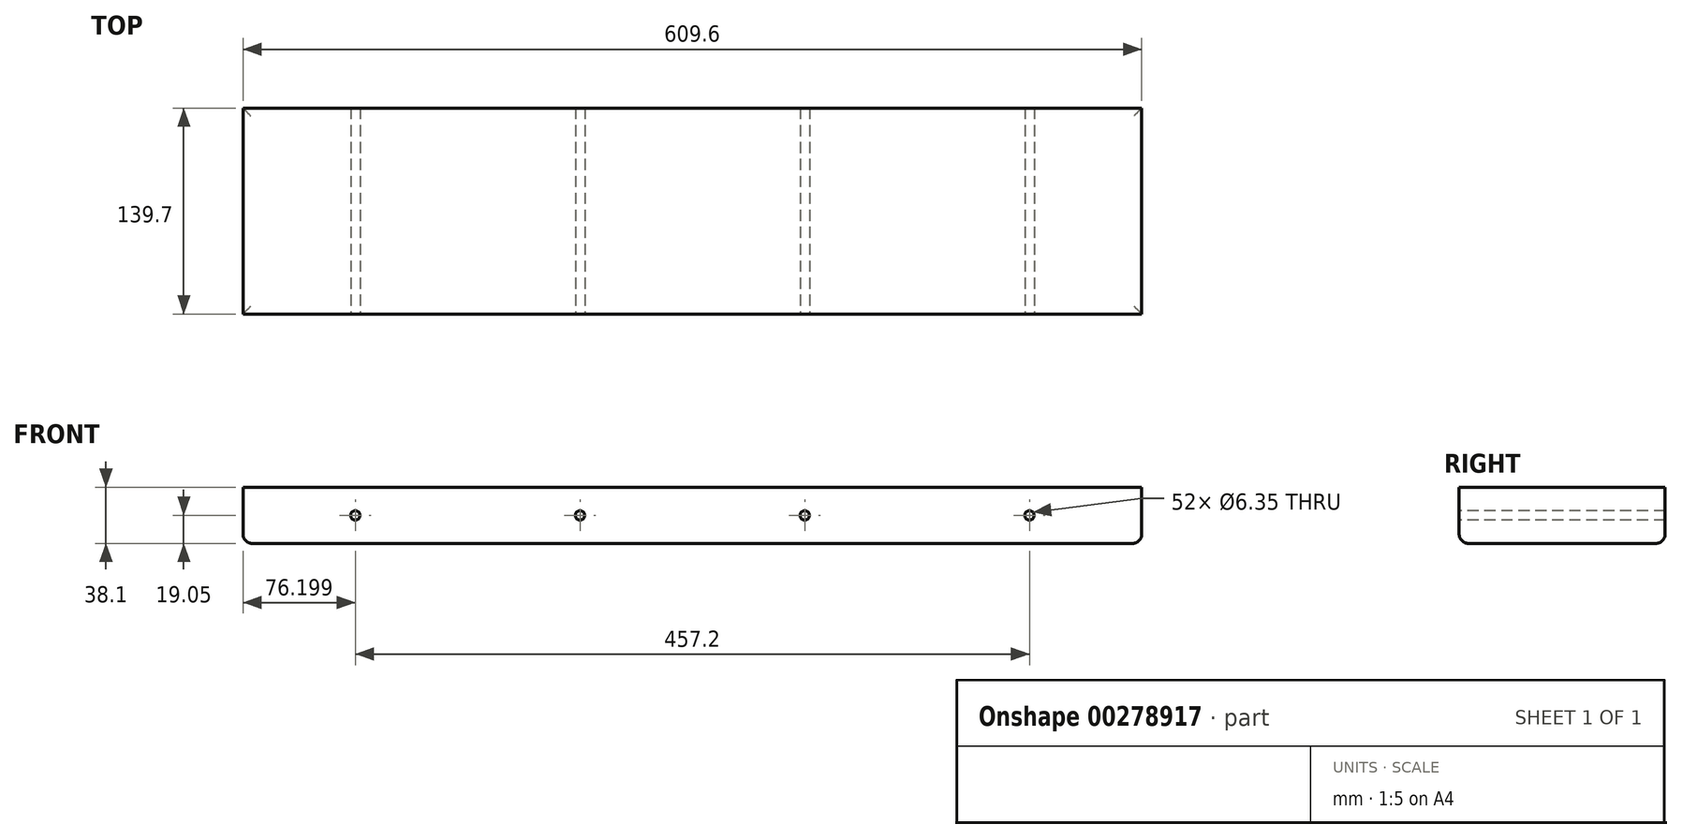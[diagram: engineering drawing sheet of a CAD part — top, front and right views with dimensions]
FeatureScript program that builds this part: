
annotation { "Feature Type Name" : "Feature", "Feature Type Description" : "" }
export const myFeature = defineFeature(function(context is Context, id is Id, definition is map)
    precondition{}
    {
        {
            var Q0;
            Q0=qCreatedBy(makeId("Top.planeOp"),FACE);
            var sketch = newSketch(context, id + "F3", { "sketchPlane" : qUnion([Q0])});
            skLineSegment(sketch, "E0.bottom", {"start": v(-233.42, 0) * mm, "end": v(376.18, 0) * mm});
            skLineSegment(sketch, "E0.top", {"start": v(-233.42, -139.7) * mm, "end": v(376.18, -139.7) * mm});
            skLineSegment(sketch, "E0.left", {"start": v(-233.42, 0) * mm, "end": v(-233.42, -139.7) * mm});
            skLineSegment(sketch, "E0.right", {"start": v(376.18, 0) * mm, "end": v(376.18, -139.7) * mm});
            skSolve(sketch);
        }
        {
            var Q0;
            Q0=qSketchRegion(id+"F3",true);
            extrude(context, id + "F0", {"entities" : qUnion([Q0]), "depth" : 38.1 * mm});
        }
        {
            var Q0;
            Q0=makeQuery(id+"F0.opExtrude","SWEPT_FACE",FACE,{"disambiguationData":[OSD([sQuery(id+"F3.wireOp",EDGE,"E0.top")])]});
            var sketch = newSketch(context, id + "F1", { "sketchPlane" : qUnion([Q0])});
            skCircle(sketch, "E1", {"center": v(-157.22, 19.05) * mm, "radius": 3.18 * mm});
            skCircle(sketch, "E2.1.0.0", {"center": v(-4.82, 19.05) * mm, "radius": 3.18 * mm});
            skCircle(sketch, "E2.2.0.0", {"center": v(147.58, 19.05) * mm, "radius": 3.18 * mm});
            skCircle(sketch, "E2.3.0.0", {"center": v(299.98, 19.05) * mm, "radius": 3.18 * mm});
            skLineSegment(sketch, "E2.direction1", {"start": v(-157.22, 19.05) * mm, "end": v(-4.82, 19.05) * mm, "construction": true});
            skSolve(sketch);
        }
        {
            var Q0;
            Q0=qSketchRegion(id+"F1",true);
            extrude(context, id + "F4", {"entities" : qUnion([Q0]), "operationType" : NewBodyOperationType.REMOVE, "oppositeDirection" : true, "depth" : 139.7 * mm});
        }
        {
            var Q0;
            Q0=makeQuery(id+"F0.opExtrude","CAP_EDGE",EDGE,{"disambiguationData":[OSD([sQuery(id+"F3.wireOp",EDGE,"E0.top")])],"isStart":true});
            var Q1;
            Q1=makeQuery(id+"F0.opExtrude","CAP_FACE",FACE,{"disambiguationData":[OSD([sQuery(id+"F3.wireOp",EDGE,"E0.bottom"),sQuery(id+"F3.wireOp",EDGE,"E0.top"),sQuery(id+"F3.wireOp",EDGE,"E0.left"),sQuery(id+"F3.wireOp",EDGE,"E0.right")])],"isStart":true});
            fillet(context, id + "F2", {"entities" : qUnion([Q0, Q1]), "radius" : 6.35 * mm, "tangentPropagation" : true, "allowEdgeOverflow" : false});
        }
    });
